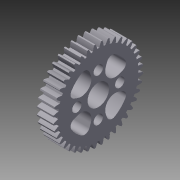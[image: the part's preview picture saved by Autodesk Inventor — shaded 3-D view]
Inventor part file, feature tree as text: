
AUTODESK INVENTOR PART (.ipt)
format: ipt  version: 2014 SP1 (Build 180222100, 222)  size: 366,080 bytes
history: native  units: in
note: dims shown in document units (in); Inventor stores cm internally (conversion verified against a paired STEP export)
features: imported_body x1, extrude x1, fillet x1, pattern_circular x1, sketch x1
ambient origin geometry x8: Origin, YZ Plane, XZ Plane, XY Plane, X Axis, Y Axis, Z Axis, Center Point
bodies: Solid1 (feature_tree)
feature tree (5):
  imported_body  "Base1"
  extrude  "Extrusion1"  Depth=0.1374in
  fillet  "Fillet1"  Radius=0.1374in
  pattern_circular  "Circular Pattern1"  [2 undecoded]
  sketch  "Sketch1"  dims[d0=0.125in d1=0.1374in d2=0.1374in d3=0.15in d4=0.3937in d5=0.0in d6=0.0787in d7=1.5748in d8=360.0deg]
note: 2 required parameter values undecoded (feature->parameter linkage not recoverable at this tier; creation-order binding heuristic only, values carry confidence <= 0.55)
